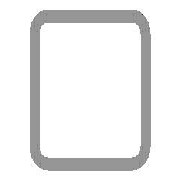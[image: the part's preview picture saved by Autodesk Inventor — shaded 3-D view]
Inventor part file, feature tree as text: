
AUTODESK INVENTOR PART (.ipt)
format: ipt  version: 2021 (Build 250183000, 183)  size: 144,896 bytes
history: native  units: mm (DEFAULTED — no unit token found)
features: other x5, sketch x3, extrude x1, split x1, plane x1
ambient origin geometry x8: Origin, YZ Plane, XZ Plane, XY Plane, X Axis, Y Axis, Z Axis, Center Point
bodies: Solid1 (feature_tree)
feature tree (11):
  parser-record x1  (decoder bookkeeping rows leaked as tree rows — omitted from the tree; the rows remain in map.json)
  other  "Driven Length"
  other  "Plano inicial"
  other  "Plano final"
  extrude  "Corpo"  TaperAngle=0.0deg  [1 undecoded]
  other  "Plano de trabalho4"
  split  "Dividir1"
  sketch  "Esboço"  dims[d11=50.8mm d12=4.7625mm d13=-21.761467mm d14=1000.0mm d15=25.4mm d16=25.4mm d17=9.525mm d18=90.0deg d19=1021.761467mm]
  sketch  "Sketch3"  dims[d3=1021.761467mm d4=0.0mm]
  plane  "Work Plane3"
  sketch  "Sketch4"  dims[d10=50.8mm]
note: 1 required parameter value undecoded (feature->parameter linkage not recoverable at this tier; creation-order binding heuristic only, values carry confidence <= 0.55)
